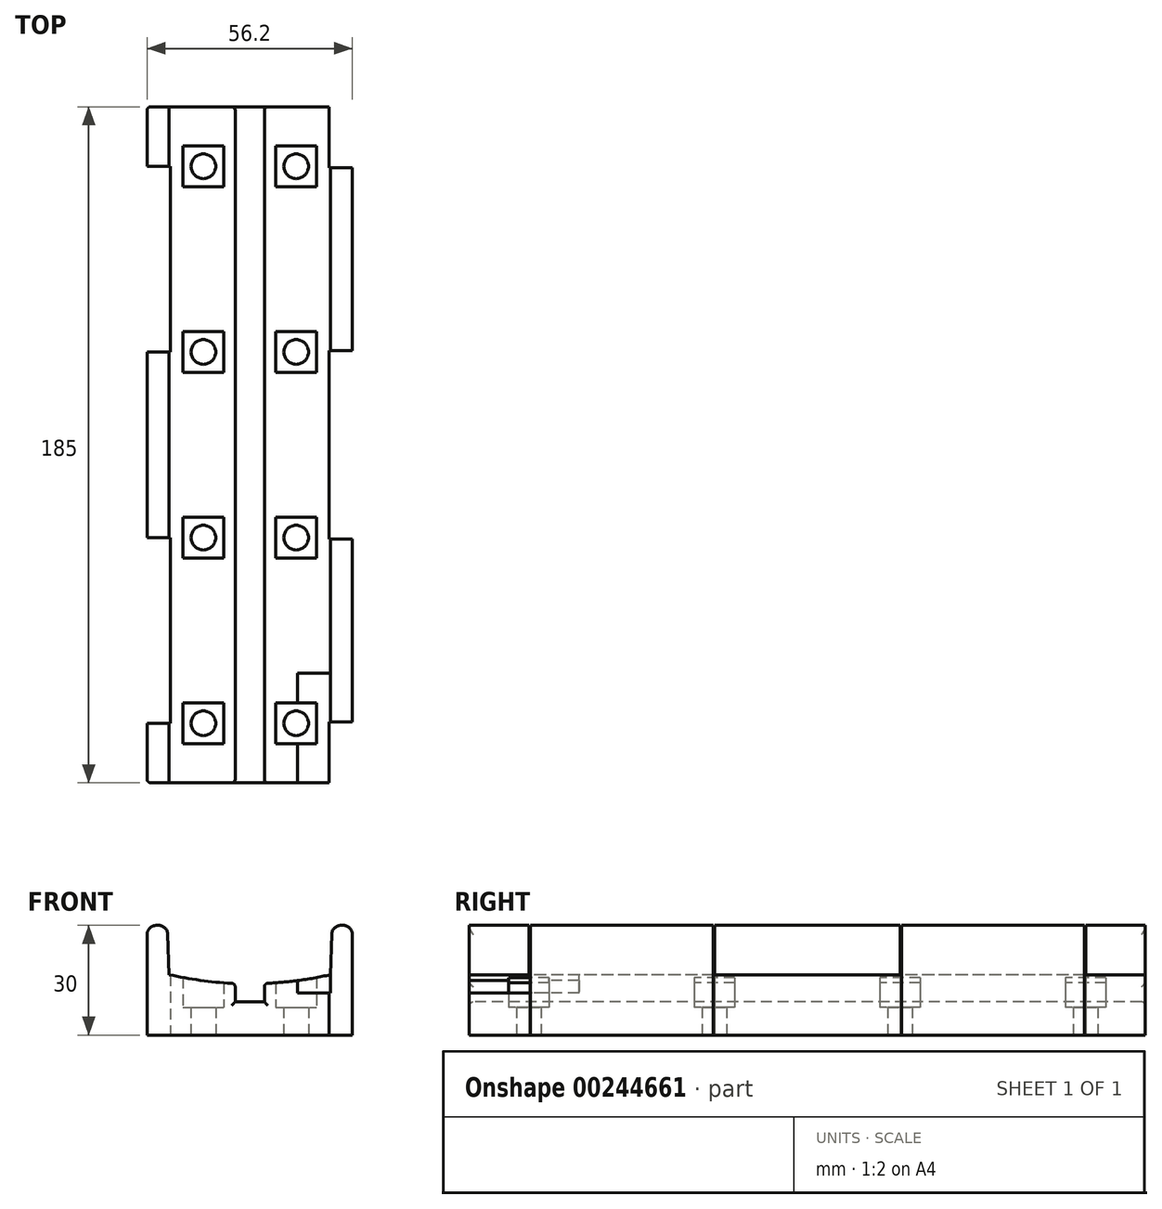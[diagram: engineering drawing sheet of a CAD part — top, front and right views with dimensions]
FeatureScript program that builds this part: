
annotation { "Feature Type Name" : "Feature", "Feature Type Description" : "" }
export const myFeature = defineFeature(function(context is Context, id is Id, definition is map)
    precondition{}
    {
        {
            var Q0;
            Q0=qCreatedBy(makeId("Front.planeOp"),FACE);
            var sketch = newSketch(context, id + "F0", { "sketchPlane" : qUnion([Q0])});
            skCircle(sketch, "E0", {"center": v(0, 0) * mm, "radius": 100.1 * mm});
            skLineSegment(sketch, "E1", {"start": v(0, 0) * mm, "end": v(0, -100.1) * mm});
            skLineSegment(sketch, "E2", {"start": v(0, -97.64) * mm, "end": v(22.05, -97.64) * mm});
            skLineSegment(sketch, "E3", {"start": v(0, -97.64) * mm, "end": v(-22.05, -97.64) * mm});
            skLineSegment(sketch, "E4", {"start": v(0, 0) * mm, "end": v(0, -27.77) * mm});
            skLineSegment(sketch, "E5", {"start": v(0, 0) * mm, "end": v(0, -84.15) * mm});
            skLineSegment(sketch, "E6", {"start": v(0, -84.15) * mm, "end": v(22.52, -84.15) * mm});
            skLineSegment(sketch, "E7", {"start": v(22.52, -84.15) * mm, "end": v(22.05, -97.64) * mm});
            skLineSegment(sketch, "E8", {"start": v(0, -84.15) * mm, "end": v(-22.52, -84.15) * mm});
            skLineSegment(sketch, "E9", {"start": v(-22.52, -84.15) * mm, "end": v(-22.05, -97.64) * mm});
            skLineSegment(sketch, "E10", {"start": v(-22.52, -84.15) * mm, "end": v(-28.1, -84.15) * mm});
            skLineSegment(sketch, "E11", {"start": v(-28.1, -84.15) * mm, "end": v(-28.1, -104.15) * mm});
            skLineSegment(sketch, "E12", {"start": v(-28.1, -104.15) * mm, "end": v(-48.1, -104.15) * mm});
            skLineSegment(sketch, "E13", {"start": v(-48.1, -104.15) * mm, "end": v(-48.1, -114.15) * mm});
            skLineSegment(sketch, "E14", {"start": v(-48.1, -114.15) * mm, "end": v(0, -114.15) * mm});
            skLineSegment(sketch, "E15", {"start": v(0, -114.15) * mm, "end": v(48.1, -114.15) * mm});
            skLineSegment(sketch, "E16", {"start": v(48.1, -114.15) * mm, "end": v(48.1, -104.15) * mm});
            skLineSegment(sketch, "E17", {"start": v(0, -97.64) * mm, "end": v(4, -97.64) * mm});
            skLineSegment(sketch, "E18", {"start": v(4, -105.1) * mm, "end": v(-4, -105.1) * mm});
            skLineSegment(sketch, "E19", {"start": v(-4, -105.1) * mm, "end": v(-4, -97.64) * mm});
            skLineSegment(sketch, "E20", {"start": v(4, -105.1) * mm, "end": v(4, -97.64) * mm});
            skLineSegment(sketch, "E21", {"start": v(22.05, -97.64) * mm, "end": v(13.05, -97.64) * mm});
            skLineSegment(sketch, "E22", {"start": v(13.05, -97.64) * mm, "end": v(13.05, -102.64) * mm});
            skLineSegment(sketch, "E23", {"start": v(13.05, -102.64) * mm, "end": v(22.05, -102.64) * mm});
            skLineSegment(sketch, "E24", {"start": v(22.05, -102.64) * mm, "end": v(22.05, -97.64) * mm});
            skLineSegment(sketch, "E25", {"start": v(22.52, -84.15) * mm, "end": v(28.1, -84.15) * mm});
            skLineSegment(sketch, "E26", {"start": v(28.1, -84.15) * mm, "end": v(28.1, -104.15) * mm});
            skLineSegment(sketch, "E27", {"start": v(28.1, -104.15) * mm, "end": v(48.1, -104.15) * mm});
            skLineSegment(sketch, "E28", {"start": v(-28.1, -104.15) * mm, "end": v(-28.1, -114.15) * mm});
            skLineSegment(sketch, "E29", {"start": v(28.1, -104.15) * mm, "end": v(28.1, -114.15) * mm});
            skSolve(sketch);
        }
        {
            var Q0;
            {var subQ0=sQuery(id+"F0.wireOp",EDGE,"E9");Q0=makeQuery(id+"F0.imprint","IMPRINT",FACE,{"disambiguationData":[TD([[makeQuery(id+"F0.imprint","IMPRINT",EDGE,{"derivedFrom":subQ0}),-1.0]])]});}
            var Q1;
            {var subQ0=sQuery(id+"F0.wireOp",EDGE,"E7");Q1=makeQuery(id+"F0.imprint","IMPRINT",FACE,{"disambiguationData":[TD([[makeQuery(id+"F0.imprint","IMPRINT",EDGE,{"derivedFrom":subQ0}),1.0]])]});}
            var Q2;
            {var subQ4=sQuery(id+"F0.wireOp",EDGE,"E23");Q2=makeQuery(id+"F0.imprint","IMPRINT",FACE,{"disambiguationData":[TD([[makeQuery(id+"F0.imprint","IMPRINT",EDGE,{"derivedFrom":subQ4}),1.0]])]});}
            var Q3;
            {var subQ1=sQuery(id+"F0.wireOp",EDGE,"E18");Q3=makeQuery(id+"F0.imprint","IMPRINT",FACE,{"disambiguationData":[TD([[makeQuery(id+"F0.imprint","IMPRINT",EDGE,{"derivedFrom":subQ1}),1.0]])]});}
            extrude(context, id + "F1", {"entities" : qUnion([Q0, Q1, Q2, Q3]), "oppositeDirection" : true, "depth" : 185 * mm});
        }
        {
            var Q0;
            Q0=makeQuery(id+"F1.opExtrude","SWEPT_FACE",FACE,{"disambiguationData":[OSD([sQuery(id+"F0.wireOp",EDGE,"E14"),sQuery(id+"F0.wireOp",EDGE,"E15")])]});
            var sketch = newSketch(context, id + "F2", { "sketchPlane" : qUnion([Q0])});
            skLineSegment(sketch, "E30", {"start": v(0, 0) * mm, "end": v(-12.7, 0) * mm});
            skLineSegment(sketch, "E31", {"start": v(-12.7, 0) * mm, "end": v(-25.4, 0) * mm});
            skLineSegment(sketch, "E32", {"start": v(0, 0) * mm, "end": v(12.7, 0) * mm});
            skPoint(sketch, "E33.endSnap0", {"position": v(6.35, 0) * mm});
            skLineSegment(sketch, "E34", {"start": v(-12.7, 0) * mm, "end": v(-12.7, -185) * mm});
            skLineSegment(sketch, "E35", {"start": v(12.7, 0) * mm, "end": v(12.7, -185) * mm});
            skLineSegment(sketch, "E36", {"start": v(0, 0) * mm, "end": v(0, -16.3) * mm});
            skLineSegment(sketch, "E37", {"start": v(0, -16.3) * mm, "end": v(0, -67.1) * mm});
            skLineSegment(sketch, "E38", {"start": v(0, -67.1) * mm, "end": v(0, -117.9) * mm});
            skLineSegment(sketch, "E39", {"start": v(0, -117.9) * mm, "end": v(0, -168.7) * mm});
            skLineSegment(sketch, "E40", {"start": v(-12.7, -16.3) * mm, "end": v(12.7, -16.3) * mm});
            skLineSegment(sketch, "E41", {"start": v(-12.7, -67.1) * mm, "end": v(12.7, -67.1) * mm});
            skLineSegment(sketch, "E42", {"start": v(-12.7, -117.9) * mm, "end": v(12.7, -117.9) * mm});
            skLineSegment(sketch, "E43", {"start": v(-12.7, -168.7) * mm, "end": v(12.7, -168.7) * mm});
            skLineSegment(sketch, "E44", {"start": v(-28.1, -117.9) * mm, "end": v(-28.1, -168.7) * mm});
            skLineSegment(sketch, "E45", {"start": v(-28.1, -16.3) * mm, "end": v(-28.1, -67.1) * mm});
            skLineSegment(sketch, "E46", {"start": v(28.1, -16.7) * mm, "end": v(28.1, 0) * mm});
            skLineSegment(sketch, "E47", {"start": v(21.77, -66.7) * mm, "end": v(28.1, -66.7) * mm});
            skLineSegment(sketch, "E48", {"start": v(28.1, -66.7) * mm, "end": v(28.1, -118.3) * mm});
            skLineSegment(sketch, "E49", {"start": v(28.1, -118.3) * mm, "end": v(21.77, -118.3) * mm});
            skLineSegment(sketch, "E50", {"start": v(21.77, -118.3) * mm, "end": v(21.77, -66.7) * mm});
            skLineSegment(sketch, "E51", {"start": v(28.1, -168.3) * mm, "end": v(28.1, -185) * mm});
            skLineSegment(sketch, "E52", {"start": v(28.1, -16.7) * mm, "end": v(21.77, -16.7) * mm});
            skLineSegment(sketch, "E53", {"start": v(21.77, -16.7) * mm, "end": v(21.77, 0) * mm});
            skLineSegment(sketch, "E54", {"start": v(21.77, 0) * mm, "end": v(28.1, 0) * mm});
            skLineSegment(sketch, "E55", {"start": v(28.1, -168.3) * mm, "end": v(21.77, -168.3) * mm});
            skLineSegment(sketch, "E56", {"start": v(21.77, -168.3) * mm, "end": v(21.77, -185) * mm});
            skLineSegment(sketch, "E57", {"start": v(21.77, -185) * mm, "end": v(28.1, -185) * mm});
            skLineSegment(sketch, "E58.bottom", {"start": v(-18.26, -174.26) * mm, "end": v(-7.14, -174.26) * mm});
            skLineSegment(sketch, "E58.top", {"start": v(-18.26, -163.14) * mm, "end": v(-7.14, -163.14) * mm});
            skLineSegment(sketch, "E58.left", {"start": v(-18.26, -174.26) * mm, "end": v(-18.26, -163.14) * mm});
            skLineSegment(sketch, "E58.right", {"start": v(-7.14, -174.26) * mm, "end": v(-7.14, -163.14) * mm});
            skPoint(sketch, "E58.middle", {"position": v(-12.7, -168.7) * mm});
            skLineSegment(sketch, "E59.bottom", {"start": v(7.14, -174.26) * mm, "end": v(18.26, -174.26) * mm});
            skLineSegment(sketch, "E59.top", {"start": v(7.14, -163.14) * mm, "end": v(18.26, -163.14) * mm});
            skLineSegment(sketch, "E59.left", {"start": v(7.14, -174.26) * mm, "end": v(7.14, -163.14) * mm});
            skLineSegment(sketch, "E59.right", {"start": v(18.26, -174.26) * mm, "end": v(18.26, -163.14) * mm});
            skPoint(sketch, "E59.middle", {"position": v(12.7, -168.7) * mm});
            skLineSegment(sketch, "E60.bottom", {"start": v(7.14, -123.46) * mm, "end": v(18.26, -123.46) * mm});
            skLineSegment(sketch, "E60.top", {"start": v(7.14, -112.34) * mm, "end": v(18.26, -112.34) * mm});
            skLineSegment(sketch, "E60.left", {"start": v(7.14, -123.46) * mm, "end": v(7.14, -112.34) * mm});
            skLineSegment(sketch, "E60.right", {"start": v(18.26, -123.46) * mm, "end": v(18.26, -112.34) * mm});
            skPoint(sketch, "E60.middle", {"position": v(12.7, -117.9) * mm});
            skLineSegment(sketch, "E61.bottom", {"start": v(-18.26, -123.46) * mm, "end": v(-7.14, -123.46) * mm});
            skLineSegment(sketch, "E61.top", {"start": v(-18.26, -112.34) * mm, "end": v(-7.14, -112.34) * mm});
            skLineSegment(sketch, "E61.left", {"start": v(-18.26, -123.46) * mm, "end": v(-18.26, -112.34) * mm});
            skLineSegment(sketch, "E61.right", {"start": v(-7.14, -123.46) * mm, "end": v(-7.14, -112.34) * mm});
            skPoint(sketch, "E61.middle", {"position": v(-12.7, -117.9) * mm});
            skLineSegment(sketch, "E62.bottom", {"start": v(7.14, -72.66) * mm, "end": v(18.26, -72.66) * mm});
            skLineSegment(sketch, "E62.top", {"start": v(7.14, -61.54) * mm, "end": v(18.26, -61.54) * mm});
            skLineSegment(sketch, "E62.left", {"start": v(7.14, -72.66) * mm, "end": v(7.14, -61.54) * mm});
            skLineSegment(sketch, "E62.right", {"start": v(18.26, -72.66) * mm, "end": v(18.26, -61.54) * mm});
            skPoint(sketch, "E62.middle", {"position": v(12.7, -67.1) * mm});
            skLineSegment(sketch, "E63.bottom", {"start": v(-18.26, -72.66) * mm, "end": v(-7.14, -72.66) * mm});
            skLineSegment(sketch, "E63.top", {"start": v(-18.26, -61.54) * mm, "end": v(-7.14, -61.54) * mm});
            skLineSegment(sketch, "E63.left", {"start": v(-18.26, -72.66) * mm, "end": v(-18.26, -61.54) * mm});
            skLineSegment(sketch, "E63.right", {"start": v(-7.14, -72.66) * mm, "end": v(-7.14, -61.54) * mm});
            skPoint(sketch, "E63.middle", {"position": v(-12.7, -67.1) * mm});
            skLineSegment(sketch, "E64.bottom", {"start": v(7.14, -21.86) * mm, "end": v(18.26, -21.86) * mm});
            skLineSegment(sketch, "E64.top", {"start": v(7.14, -10.74) * mm, "end": v(18.26, -10.74) * mm});
            skLineSegment(sketch, "E64.left", {"start": v(7.14, -21.86) * mm, "end": v(7.14, -10.74) * mm});
            skLineSegment(sketch, "E64.right", {"start": v(18.26, -21.86) * mm, "end": v(18.26, -10.74) * mm});
            skPoint(sketch, "E64.middle", {"position": v(12.7, -16.3) * mm});
            skLineSegment(sketch, "E65.bottom", {"start": v(-18.26, -21.86) * mm, "end": v(-7.14, -21.86) * mm});
            skLineSegment(sketch, "E65.top", {"start": v(-18.26, -10.74) * mm, "end": v(-7.14, -10.74) * mm});
            skLineSegment(sketch, "E65.left", {"start": v(-18.26, -21.86) * mm, "end": v(-18.26, -10.74) * mm});
            skLineSegment(sketch, "E65.right", {"start": v(-7.14, -21.86) * mm, "end": v(-7.14, -10.74) * mm});
            skPoint(sketch, "E65.middle", {"position": v(-12.7, -16.3) * mm});
            skLineSegment(sketch, "E66", {"start": v(-28.1, -67.1) * mm, "end": v(-21.77, -67.1) * mm});
            skLineSegment(sketch, "E67", {"start": v(-21.77, -67.1) * mm, "end": v(-21.77, -16.3) * mm});
            skLineSegment(sketch, "E68", {"start": v(-21.77, -16.3) * mm, "end": v(-28.1, -16.3) * mm});
            skLineSegment(sketch, "E69", {"start": v(-28.1, -168.7) * mm, "end": v(-21.77, -168.7) * mm});
            skLineSegment(sketch, "E70", {"start": v(-21.77, -168.7) * mm, "end": v(-21.77, -117.9) * mm});
            skLineSegment(sketch, "E71", {"start": v(-21.77, -117.9) * mm, "end": v(-28.1, -117.9) * mm});
            skSolve(sketch);
        }
        {
            var Q0;
            {var subQ4=sQuery(id+"F0.wireOp",EDGE,"E23");Q0=makeQuery(id+"F0.imprint","IMPRINT",FACE,{"disambiguationData":[TD([[makeQuery(id+"F0.imprint","IMPRINT",EDGE,{"derivedFrom":subQ4}),1.0]])]});}
            extrude(context, id + "F3", {"entities" : qUnion([Q0]), "operationType" : NewBodyOperationType.REMOVE, "oppositeDirection" : true, "depth" : 30 * mm});
        }
        {
            var Q0;
            Q0=makeQuery(id+"F2.imprint","IMPRINT",FACE,{"disambiguationData":[TD([[makeQuery(id+"F2.imprint","IMPRINT",EDGE,{"derivedFrom":sQuery(id+"F2.wireOp",EDGE,"ExksGU1t-qP8x-1NmI-xvym-EXXfxOyielZT")}),-1.0]])]});
            var Q1;
            Q1=makeQuery(id+"F2.imprint","IMPRINT",FACE,{"disambiguationData":[TD([[makeQuery(id+"F2.imprint","IMPRINT",EDGE,{"derivedFrom":sQuery(id+"F2.wireOp",EDGE,"Dlua8FRt-CBCO-nQll-GRtb-0ZUc91wX2NCH")}),1.0]])]});
            var Q2;
            Q2=makeQuery(id+"F2.imprint","IMPRINT",FACE,{"disambiguationData":[TD([[makeQuery(id+"F2.imprint","IMPRINT",EDGE,{"derivedFrom":sQuery(id+"F2.wireOp",EDGE,"U0LU0WGO-nAsz-9quZ-7W6P-sSRSlS0zgo32")}),1.0]])]});
            var Q3;
            Q3=makeQuery(id+"F2.imprint","IMPRINT",FACE,{"disambiguationData":[TD([[makeQuery(id+"F2.imprint","IMPRINT",EDGE,{"derivedFrom":sQuery(id+"F2.wireOp",EDGE,"Mpgb5OfM-xtKE-B3vf-NreA-cOOLYNg0Ylo6")}),-1.0]])]});
            var Q4;
            Q4=makeQuery(id+"F2.imprint","IMPRINT",FACE,{"disambiguationData":[TD([[makeQuery(id+"F2.imprint","IMPRINT",EDGE,{"derivedFrom":sQuery(id+"F2.wireOp",EDGE,"aVloRQdx-kqiO-uwB9-Mu7t-cq4rksKn9tI0")}),1.0]])]});
            var Q5;
            Q5=makeQuery(id+"F2.imprint","IMPRINT",FACE,{"disambiguationData":[TD([[makeQuery(id+"F2.imprint","IMPRINT",EDGE,{"derivedFrom":sQuery(id+"F2.wireOp",EDGE,"JxgklWCk-fe55-kQkM-h4Wt-7ELSXvmmRhvv")}),-1.0]])]});
            var Q6;
            Q6=makeQuery(id+"F2.imprint","IMPRINT",FACE,{"disambiguationData":[TD([[makeQuery(id+"F2.imprint","IMPRINT",EDGE,{"derivedFrom":sQuery(id+"F2.wireOp",EDGE,"E47")}),-1.0]])]});
            var Q7;
            Q7=makeQuery(id+"F2.imprint","IMPRINT",FACE,{"disambiguationData":[TD([[makeQuery(id+"F2.imprint","IMPRINT",EDGE,{"derivedFrom":sQuery(id+"F2.wireOp",EDGE,"U4hY8Gpc-lZY6-V4IC-H5w9-8qsGqMVm0EJW")}),1.0]])]});
            var Q8;
            Q8=makeQuery(id+"F2.imprint","IMPRINT",FACE,{"disambiguationData":[TD([[makeQuery(id+"F2.imprint","IMPRINT",EDGE,{"derivedFrom":sQuery(id+"F2.wireOp",EDGE,"E51")}),1.0]])]});
            var Q9;
            Q9=makeQuery(id+"F2.imprint","IMPRINT",FACE,{"disambiguationData":[TD([[makeQuery(id+"F2.imprint","IMPRINT",EDGE,{"derivedFrom":sQuery(id+"F2.wireOp",EDGE,"E46")}),1.0]])]});
            var Q10;
            Q10=makeQuery(id+"F2.imprint","IMPRINT",FACE,{"disambiguationData":[TD([[makeQuery(id+"F2.imprint","IMPRINT",EDGE,{"derivedFrom":sQuery(id+"F2.wireOp",EDGE,"E44")}),-1.0]])]});
            var Q11;
            Q11=makeQuery(id+"F2.imprint","IMPRINT",FACE,{"disambiguationData":[TD([[makeQuery(id+"F2.imprint","IMPRINT",EDGE,{"derivedFrom":sQuery(id+"F2.wireOp",EDGE,"E45")}),-1.0]])]});
            extrude(context, id + "F4", {"entities" : qUnion([Q0, Q1, Q2, Q3, Q4, Q5, Q6, Q7, Q8, Q9, Q10, Q11]), "operationType" : NewBodyOperationType.REMOVE, "endBound" : BoundingType.UP_TO_NEXT, "oppositeDirection" : true, "depth" : 30 * mm});
        }
        {
            var Q0;
            Q0=sQuery(id+"F2.wireOp",VERTEX,"E43.start");
            var Q1;
            Q1=sQuery(id+"F2.wireOp",VERTEX,"E43.end");
            var Q2;
            Q2=sQuery(id+"F2.wireOp",VERTEX,"E42.start");
            var Q3;
            Q3=sQuery(id+"F2.wireOp",VERTEX,"E42.end");
            var Q4;
            Q4=sQuery(id+"F2.wireOp",VERTEX,"E41.start");
            var Q5;
            Q5=sQuery(id+"F2.wireOp",VERTEX,"E41.end");
            var Q6;
            Q6=sQuery(id+"F2.wireOp",VERTEX,"E40.start");
            var Q7;
            Q7=sQuery(id+"F2.wireOp",VERTEX,"E40.end");
            var Q8;
            Q8=makeQuery(id+"F1.opExtrude","SWEPT_BODY",BODY,{"disambiguationData":[OSD([sQuery(id+"F0.wireOp",EDGE,"E0"),sQuery(id+"F0.wireOp",EDGE,"E7"),sQuery(id+"F0.wireOp",EDGE,"E9"),sQuery(id+"F0.wireOp",EDGE,"E10"),sQuery(id+"F0.wireOp",EDGE,"E11"),sQuery(id+"F0.wireOp",EDGE,"E14"),sQuery(id+"F0.wireOp",EDGE,"E15"),sQuery(id+"F0.wireOp",EDGE,"E18"),sQuery(id+"F0.wireOp",EDGE,"E19"),sQuery(id+"F0.wireOp",EDGE,"E20"),sQuery(id+"F0.wireOp",EDGE,"E25"),sQuery(id+"F0.wireOp",EDGE,"E26"),sQuery(id+"F0.wireOp",EDGE,"E28"),sQuery(id+"F0.wireOp",EDGE,"E29")])]});
            hole(context, id + "F5", {"style" : HoleStyle.SIMPLE, "endStyle" : HoleEndStyle.THROUGH, "standardTappedOrClearance" : lookupTablePath({ "standard" : "ANSI", "fit" : "Normal (ASME)", "size" : "1/4", "type" : "Clearance" }), "standardBlindInLast" : lookupTablePath({ "fit" : "Free", "standard" : "ANSI", "size" : "1/4", "type" : "Clearance" }), "holeDiameter" : 6.76 * mm, "tappedDepth" : 12 * mm, "tapClearance" : 3, "locations" : qUnion([Q0, Q1, Q2, Q3, Q4, Q5, Q6, Q7]), "scope" : qUnion([Q8])});
        }
        {
            var Q0;
            {var subQ0=sQuery(id+"F2.wireOp",EDGE,"E58.left");Q0=makeQuery(id+"F2.imprint","IMPRINT",FACE,{"disambiguationData":[TD([[makeQuery(id+"F2.imprint","IMPRINT",EDGE,{"derivedFrom":subQ0}),-1.0]])]});}
            var Q1;
            {var subQ0=sQuery(id+"F2.wireOp",EDGE,"E43");var subQ1=sQuery(id+"F2.wireOp",EDGE,"E34");var subQ2=makeQuery(id+"F2.imprint","INTERSECT",VERTEX,{"derivedFrom":[subQ1,subQ0]});Q1=makeQuery(id+"F2.imprint","IMPRINT",FACE,{"disambiguationData":[TD([[makeQuery(id+"F2.imprint","IMPRINT",EDGE,{"disambiguationData":[TD([[subQ2,1.0]])],"derivedFrom":subQ1}),1.0]])]});}
            var Q2;
            {var subQ0=sQuery(id+"F2.wireOp",EDGE,"E43");var subQ1=sQuery(id+"F2.wireOp",EDGE,"E34");var subQ2=makeQuery(id+"F2.imprint","INTERSECT",VERTEX,{"derivedFrom":[subQ1,subQ0]});Q2=makeQuery(id+"F2.imprint","IMPRINT",FACE,{"disambiguationData":[TD([[makeQuery(id+"F2.imprint","IMPRINT",EDGE,{"disambiguationData":[TD([[subQ2,-1.0]])],"derivedFrom":subQ1}),1.0]])]});}
            var Q3;
            {var subQ0=sQuery(id+"F2.wireOp",EDGE,"E43");var subQ1=sQuery(id+"F2.wireOp",EDGE,"E35");var subQ2=makeQuery(id+"F2.imprint","INTERSECT",VERTEX,{"derivedFrom":[subQ1,subQ0]});Q3=makeQuery(id+"F2.imprint","IMPRINT",FACE,{"disambiguationData":[TD([[makeQuery(id+"F2.imprint","IMPRINT",EDGE,{"disambiguationData":[TD([[subQ2,-1.0]])],"derivedFrom":subQ1}),-1.0]])]});}
            var Q4;
            {var subQ0=sQuery(id+"F2.wireOp",EDGE,"E43");var subQ1=sQuery(id+"F2.wireOp",EDGE,"E35");var subQ2=makeQuery(id+"F2.imprint","INTERSECT",VERTEX,{"derivedFrom":[subQ1,subQ0]});Q4=makeQuery(id+"F2.imprint","IMPRINT",FACE,{"disambiguationData":[TD([[makeQuery(id+"F2.imprint","IMPRINT",EDGE,{"disambiguationData":[TD([[subQ2,1.0]])],"derivedFrom":subQ1}),-1.0]])]});}
            var Q5;
            {var subQ0=sQuery(id+"F2.wireOp",EDGE,"E59.right");Q5=makeQuery(id+"F2.imprint","IMPRINT",FACE,{"disambiguationData":[TD([[makeQuery(id+"F2.imprint","IMPRINT",EDGE,{"derivedFrom":subQ0}),1.0]])]});}
            var Q6;
            {var subQ0=sQuery(id+"F2.wireOp",EDGE,"E60.right");Q6=makeQuery(id+"F2.imprint","IMPRINT",FACE,{"disambiguationData":[TD([[makeQuery(id+"F2.imprint","IMPRINT",EDGE,{"derivedFrom":subQ0}),1.0]])]});}
            var Q7;
            {var subQ0=sQuery(id+"F2.wireOp",EDGE,"E42");var subQ1=sQuery(id+"F2.wireOp",EDGE,"E35");var subQ2=makeQuery(id+"F2.imprint","INTERSECT",VERTEX,{"derivedFrom":[subQ1,subQ0]});Q7=makeQuery(id+"F2.imprint","IMPRINT",FACE,{"disambiguationData":[TD([[makeQuery(id+"F2.imprint","IMPRINT",EDGE,{"disambiguationData":[TD([[subQ2,1.0]])],"derivedFrom":subQ1}),-1.0]])]});}
            var Q8;
            {var subQ0=sQuery(id+"F2.wireOp",EDGE,"E42");var subQ1=sQuery(id+"F2.wireOp",EDGE,"E35");var subQ2=makeQuery(id+"F2.imprint","INTERSECT",VERTEX,{"derivedFrom":[subQ1,subQ0]});Q8=makeQuery(id+"F2.imprint","IMPRINT",FACE,{"disambiguationData":[TD([[makeQuery(id+"F2.imprint","IMPRINT",EDGE,{"disambiguationData":[TD([[subQ2,-1.0]])],"derivedFrom":subQ1}),-1.0]])]});}
            var Q9;
            {var subQ0=sQuery(id+"F2.wireOp",EDGE,"E42");var subQ1=sQuery(id+"F2.wireOp",EDGE,"E34");var subQ2=makeQuery(id+"F2.imprint","INTERSECT",VERTEX,{"derivedFrom":[subQ1,subQ0]});Q9=makeQuery(id+"F2.imprint","IMPRINT",FACE,{"disambiguationData":[TD([[makeQuery(id+"F2.imprint","IMPRINT",EDGE,{"disambiguationData":[TD([[subQ2,-1.0]])],"derivedFrom":subQ1}),1.0]])]});}
            var Q10;
            {var subQ0=sQuery(id+"F2.wireOp",EDGE,"E42");var subQ1=sQuery(id+"F2.wireOp",EDGE,"E34");var subQ2=makeQuery(id+"F2.imprint","INTERSECT",VERTEX,{"derivedFrom":[subQ1,subQ0]});Q10=makeQuery(id+"F2.imprint","IMPRINT",FACE,{"disambiguationData":[TD([[makeQuery(id+"F2.imprint","IMPRINT",EDGE,{"disambiguationData":[TD([[subQ2,1.0]])],"derivedFrom":subQ1}),1.0]])]});}
            var Q11;
            {var subQ0=sQuery(id+"F2.wireOp",EDGE,"E61.left");Q11=makeQuery(id+"F2.imprint","IMPRINT",FACE,{"disambiguationData":[TD([[makeQuery(id+"F2.imprint","IMPRINT",EDGE,{"derivedFrom":subQ0}),-1.0]])]});}
            var Q12;
            {var subQ0=sQuery(id+"F2.wireOp",EDGE,"E41");var subQ1=sQuery(id+"F2.wireOp",EDGE,"E34");var subQ2=makeQuery(id+"F2.imprint","INTERSECT",VERTEX,{"derivedFrom":[subQ1,subQ0]});Q12=makeQuery(id+"F2.imprint","IMPRINT",FACE,{"disambiguationData":[TD([[makeQuery(id+"F2.imprint","IMPRINT",EDGE,{"disambiguationData":[TD([[subQ2,1.0]])],"derivedFrom":subQ1}),1.0]])]});}
            var Q13;
            {var subQ0=sQuery(id+"F2.wireOp",EDGE,"E41");var subQ1=sQuery(id+"F2.wireOp",EDGE,"E34");var subQ2=makeQuery(id+"F2.imprint","INTERSECT",VERTEX,{"derivedFrom":[subQ1,subQ0]});Q13=makeQuery(id+"F2.imprint","IMPRINT",FACE,{"disambiguationData":[TD([[makeQuery(id+"F2.imprint","IMPRINT",EDGE,{"disambiguationData":[TD([[subQ2,-1.0]])],"derivedFrom":subQ1}),1.0]])]});}
            var Q14;
            {var subQ0=sQuery(id+"F2.wireOp",EDGE,"E63.left");Q14=makeQuery(id+"F2.imprint","IMPRINT",FACE,{"disambiguationData":[TD([[makeQuery(id+"F2.imprint","IMPRINT",EDGE,{"derivedFrom":subQ0}),-1.0]])]});}
            var Q15;
            {var subQ0=sQuery(id+"F2.wireOp",EDGE,"E41");var subQ1=sQuery(id+"F2.wireOp",EDGE,"E35");var subQ2=makeQuery(id+"F2.imprint","INTERSECT",VERTEX,{"derivedFrom":[subQ1,subQ0]});Q15=makeQuery(id+"F2.imprint","IMPRINT",FACE,{"disambiguationData":[TD([[makeQuery(id+"F2.imprint","IMPRINT",EDGE,{"disambiguationData":[TD([[subQ2,1.0]])],"derivedFrom":subQ1}),-1.0]])]});}
            var Q16;
            {var subQ0=sQuery(id+"F2.wireOp",EDGE,"E41");var subQ1=sQuery(id+"F2.wireOp",EDGE,"E35");var subQ2=makeQuery(id+"F2.imprint","INTERSECT",VERTEX,{"derivedFrom":[subQ1,subQ0]});Q16=makeQuery(id+"F2.imprint","IMPRINT",FACE,{"disambiguationData":[TD([[makeQuery(id+"F2.imprint","IMPRINT",EDGE,{"disambiguationData":[TD([[subQ2,-1.0]])],"derivedFrom":subQ1}),-1.0]])]});}
            var Q17;
            {var subQ0=sQuery(id+"F2.wireOp",EDGE,"E62.right");Q17=makeQuery(id+"F2.imprint","IMPRINT",FACE,{"disambiguationData":[TD([[makeQuery(id+"F2.imprint","IMPRINT",EDGE,{"derivedFrom":subQ0}),1.0]])]});}
            var Q18;
            {var subQ0=sQuery(id+"F2.wireOp",EDGE,"E40");var subQ1=sQuery(id+"F2.wireOp",EDGE,"E35");var subQ2=makeQuery(id+"F2.imprint","INTERSECT",VERTEX,{"derivedFrom":[subQ1,subQ0]});Q18=makeQuery(id+"F2.imprint","IMPRINT",FACE,{"disambiguationData":[TD([[makeQuery(id+"F2.imprint","IMPRINT",EDGE,{"disambiguationData":[TD([[subQ2,-1.0]])],"derivedFrom":subQ1}),-1.0]])]});}
            var Q19;
            {var subQ0=sQuery(id+"F2.wireOp",EDGE,"E40");var subQ1=sQuery(id+"F2.wireOp",EDGE,"E35");var subQ2=makeQuery(id+"F2.imprint","INTERSECT",VERTEX,{"derivedFrom":[subQ1,subQ0]});Q19=makeQuery(id+"F2.imprint","IMPRINT",FACE,{"disambiguationData":[TD([[makeQuery(id+"F2.imprint","IMPRINT",EDGE,{"disambiguationData":[TD([[subQ2,1.0]])],"derivedFrom":subQ1}),-1.0]])]});}
            var Q20;
            {var subQ0=sQuery(id+"F2.wireOp",EDGE,"E64.right");Q20=makeQuery(id+"F2.imprint","IMPRINT",FACE,{"disambiguationData":[TD([[makeQuery(id+"F2.imprint","IMPRINT",EDGE,{"derivedFrom":subQ0}),1.0]])]});}
            var Q21;
            {var subQ0=sQuery(id+"F2.wireOp",EDGE,"E40");var subQ1=sQuery(id+"F2.wireOp",EDGE,"E34");var subQ2=makeQuery(id+"F2.imprint","INTERSECT",VERTEX,{"derivedFrom":[subQ1,subQ0]});Q21=makeQuery(id+"F2.imprint","IMPRINT",FACE,{"disambiguationData":[TD([[makeQuery(id+"F2.imprint","IMPRINT",EDGE,{"disambiguationData":[TD([[subQ2,1.0]])],"derivedFrom":subQ1}),1.0]])]});}
            var Q22;
            {var subQ0=sQuery(id+"F2.wireOp",EDGE,"E65.left");Q22=makeQuery(id+"F2.imprint","IMPRINT",FACE,{"disambiguationData":[TD([[makeQuery(id+"F2.imprint","IMPRINT",EDGE,{"derivedFrom":subQ0}),-1.0]])]});}
            var Q23;
            {var subQ0=sQuery(id+"F2.wireOp",EDGE,"E40");var subQ1=sQuery(id+"F2.wireOp",EDGE,"E34");var subQ2=makeQuery(id+"F2.imprint","INTERSECT",VERTEX,{"derivedFrom":[subQ1,subQ0]});Q23=makeQuery(id+"F2.imprint","IMPRINT",FACE,{"disambiguationData":[TD([[makeQuery(id+"F2.imprint","IMPRINT",EDGE,{"disambiguationData":[TD([[subQ2,-1.0]])],"derivedFrom":subQ1}),1.0]])]});}
            extrude(context, id + "F6", {"entities" : qUnion([Q0, Q1, Q2, Q3, Q4, Q5, Q6, Q7, Q8, Q9, Q10, Q11, Q12, Q13, Q14, Q15, Q16, Q17, Q18, Q19, Q20, Q21, Q22, Q23]), "operationType" : NewBodyOperationType.REMOVE, "endBound" : BoundingType.THROUGH_ALL, "oppositeDirection" : true, "depth" : 15 * mm, "hasSecondDirection" : true, "secondDirectionOppositeDirection" : true, "secondDirectionDepth" : 7.6 * mm});
        }
        {
            var Q0;
            Q0=makeQuery(id+"F1.opExtrude","CAP_EDGE",EDGE,{"disambiguationData":[OSD([sQuery(id+"F0.wireOp",EDGE,"E18")])],"isStart":true});
            var Q1;
            Q1=makeQuery(id+"F1.opExtrude","CAP_EDGE",EDGE,{"disambiguationData":[OSD([sQuery(id+"F0.wireOp",EDGE,"E18")])],"isStart":false});
            var Q2;
            Q2=makeQuery(id+"F1.opExtrude","CAP_EDGE",EDGE,{"disambiguationData":[OSD([sQuery(id+"F0.wireOp",EDGE,"E19")])],"isStart":true});
            var Q3;
            Q3=makeQuery(id+"F1.opExtrude","CAP_EDGE",EDGE,{"disambiguationData":[OSD([sQuery(id+"F0.wireOp",EDGE,"E20")])],"isStart":true});
            var Q4;
            Q4=makeQuery(id+"F1.opExtrude","CAP_EDGE",EDGE,{"disambiguationData":[OSD([sQuery(id+"F0.wireOp",EDGE,"E19")])],"isStart":false});
            var Q5;
            Q5=makeQuery(id+"F1.opExtrude","CAP_EDGE",EDGE,{"disambiguationData":[OSD([sQuery(id+"F0.wireOp",EDGE,"E20")])],"isStart":false});
            var Q6;
            Q6=makeQuery(id+"F1.opExtrude","CAP_EDGE",EDGE,{"disambiguationData":[OSD([sQuery(id+"F0.wireOp",EDGE,"E11"),sQuery(id+"F0.wireOp",EDGE,"E28")])],"isStart":true});
            var Q7;
            Q7=makeQuery(id+"F1.opExtrude","CAP_EDGE",EDGE,{"disambiguationData":[OSD([sQuery(id+"F0.wireOp",EDGE,"E11"),sQuery(id+"F0.wireOp",EDGE,"E28")])],"isStart":false});
            var Q8;
            Q8=makeQuery(id+"F1.opExtrude","SWEPT_EDGE",EDGE,{"disambiguationData":[OSD([sQuery(id+"F0.wireOp",EDGE,"E0"),sQuery(id+"F0.wireOp",EDGE,"E19")])]});
            var Q9;
            Q9=makeQuery(id+"F1.opExtrude","SWEPT_EDGE",EDGE,{"disambiguationData":[OSD([sQuery(id+"F0.wireOp",EDGE,"E0"),sQuery(id+"F0.wireOp",EDGE,"E20")])]});
            fillet(context, id + "F7", {"entities" : qUnion([Q0, Q1, Q2, Q3, Q4, Q5, Q6, Q7, Q8, Q9]), "radius" : 1 * mm, "tangentPropagation" : true, "allowEdgeOverflow" : false});
        }
        {
            var Q0;
            {var subQ1=sQuery(id+"F0.wireOp",EDGE,"E11");var subQ2=sQuery(id+"F0.wireOp",EDGE,"E10");Q0=makeQuery(id+"F4.boolean.opBoolean","SPLIT",EDGE,{"disambiguationData":[TD([makeQuery(id+"F4.opExtrude","SWEPT_FACE",FACE,{"disambiguationData":[OSD([sQuery(id+"F2.wireOp",EDGE,"E68")])]})])],"derivedFrom":makeQuery(id+"F1.opExtrude","SWEPT_EDGE",EDGE,{"disambiguationData":[OSD([subQ2,subQ1])]})});}
            var Q1;
            {var subQ0=sQuery(id+"F0.wireOp",EDGE,"E10");var subQ1=sQuery(id+"F0.wireOp",EDGE,"E9");Q1=makeQuery(id+"F4.boolean.opBoolean","SPLIT",EDGE,{"disambiguationData":[TD([makeQuery(id+"F4.opExtrude","SWEPT_FACE",FACE,{"disambiguationData":[OSD([sQuery(id+"F2.wireOp",EDGE,"E68")])]})])],"derivedFrom":makeQuery(id+"F1.opExtrude","SWEPT_EDGE",EDGE,{"disambiguationData":[OSD([sQuery(id+"F0.wireOp",EDGE,"E8"),subQ1,subQ0])]})});}
            var Q2;
            {var subQ0=sQuery(id+"F0.wireOp",EDGE,"E9");var subQ1=sQuery(id+"F0.wireOp",EDGE,"E10");Q2=makeQuery(id+"F4.boolean.opBoolean","SPLIT",EDGE,{"disambiguationData":[TD([makeQuery(id+"F4.opExtrude","SWEPT_FACE",FACE,{"disambiguationData":[OSD([sQuery(id+"F2.wireOp",EDGE,"E66")])]})])],"derivedFrom":makeQuery(id+"F1.opExtrude","SWEPT_EDGE",EDGE,{"disambiguationData":[OSD([sQuery(id+"F0.wireOp",EDGE,"E8"),subQ0,subQ1])]})});}
            var Q3;
            {var subQ0=sQuery(id+"F0.wireOp",EDGE,"E10");var subQ1=sQuery(id+"F0.wireOp",EDGE,"E11");Q3=makeQuery(id+"F4.boolean.opBoolean","SPLIT",EDGE,{"disambiguationData":[TD([makeQuery(id+"F4.opExtrude","SWEPT_FACE",FACE,{"disambiguationData":[OSD([sQuery(id+"F2.wireOp",EDGE,"E66")])]})])],"derivedFrom":makeQuery(id+"F1.opExtrude","SWEPT_EDGE",EDGE,{"disambiguationData":[OSD([subQ0,subQ1])]})});}
            var Q4;
            {var subQ1=sQuery(id+"F0.wireOp",EDGE,"E11");var subQ2=sQuery(id+"F0.wireOp",EDGE,"E10");Q4=makeQuery(id+"F4.boolean.opBoolean","SPLIT",EDGE,{"disambiguationData":[TD([makeQuery(id+"F4.opExtrude","SWEPT_FACE",FACE,{"disambiguationData":[OSD([sQuery(id+"F2.wireOp",EDGE,"E69")])]})])],"derivedFrom":makeQuery(id+"F1.opExtrude","SWEPT_EDGE",EDGE,{"disambiguationData":[OSD([subQ2,subQ1])]})});}
            var Q5;
            {var subQ0=sQuery(id+"F0.wireOp",EDGE,"E10");var subQ1=sQuery(id+"F0.wireOp",EDGE,"E9");Q5=makeQuery(id+"F4.boolean.opBoolean","SPLIT",EDGE,{"disambiguationData":[TD([makeQuery(id+"F4.opExtrude","SWEPT_FACE",FACE,{"disambiguationData":[OSD([sQuery(id+"F2.wireOp",EDGE,"E69")])]})])],"derivedFrom":makeQuery(id+"F1.opExtrude","SWEPT_EDGE",EDGE,{"disambiguationData":[OSD([sQuery(id+"F0.wireOp",EDGE,"E8"),subQ1,subQ0])]})});}
            var Q6;
            {var subQ0=sQuery(id+"F0.wireOp",EDGE,"E7");var subQ1=sQuery(id+"F0.wireOp",EDGE,"E25");Q6=makeQuery(id+"F4.boolean.opBoolean","SPLIT",EDGE,{"disambiguationData":[TD([makeQuery(id+"F4.opExtrude","SWEPT_FACE",FACE,{"disambiguationData":[OSD([sQuery(id+"F2.wireOp",EDGE,"E49")])]})])],"derivedFrom":makeQuery(id+"F1.opExtrude","SWEPT_EDGE",EDGE,{"disambiguationData":[OSD([sQuery(id+"F0.wireOp",EDGE,"E6"),subQ0,subQ1])]})});}
            var Q7;
            {var subQ0=sQuery(id+"F0.wireOp",EDGE,"E25");var subQ1=sQuery(id+"F0.wireOp",EDGE,"E26");Q7=makeQuery(id+"F4.boolean.opBoolean","SPLIT",EDGE,{"disambiguationData":[TD([makeQuery(id+"F4.opExtrude","SWEPT_FACE",FACE,{"disambiguationData":[OSD([sQuery(id+"F2.wireOp",EDGE,"E49")])]})])],"derivedFrom":makeQuery(id+"F1.opExtrude","SWEPT_EDGE",EDGE,{"disambiguationData":[OSD([subQ0,subQ1])]})});}
            var Q8;
            {var subQ0=sQuery(id+"F0.wireOp",EDGE,"E25");var subQ1=sQuery(id+"F0.wireOp",EDGE,"E26");Q8=makeQuery(id+"F4.boolean.opBoolean","SPLIT",EDGE,{"disambiguationData":[TD([makeQuery(id+"F4.opExtrude","SWEPT_FACE",FACE,{"disambiguationData":[OSD([sQuery(id+"F2.wireOp",EDGE,"E47")])]})])],"derivedFrom":makeQuery(id+"F1.opExtrude","SWEPT_EDGE",EDGE,{"disambiguationData":[OSD([subQ0,subQ1])]})});}
            var Q9;
            {var subQ0=sQuery(id+"F0.wireOp",EDGE,"E7");var subQ1=sQuery(id+"F0.wireOp",EDGE,"E25");Q9=makeQuery(id+"F4.boolean.opBoolean","SPLIT",EDGE,{"disambiguationData":[TD([makeQuery(id+"F4.opExtrude","SWEPT_FACE",FACE,{"disambiguationData":[OSD([sQuery(id+"F2.wireOp",EDGE,"E47")])]})])],"derivedFrom":makeQuery(id+"F1.opExtrude","SWEPT_EDGE",EDGE,{"disambiguationData":[OSD([sQuery(id+"F0.wireOp",EDGE,"E6"),subQ0,subQ1])]})});}
            fillet(context, id + "F8", {"entities" : qUnion([Q0, Q1, Q2, Q3, Q4, Q5, Q6, Q7, Q8, Q9]), "radius" : 2.5 * mm, "allowEdgeOverflow" : false});
        }
    });
